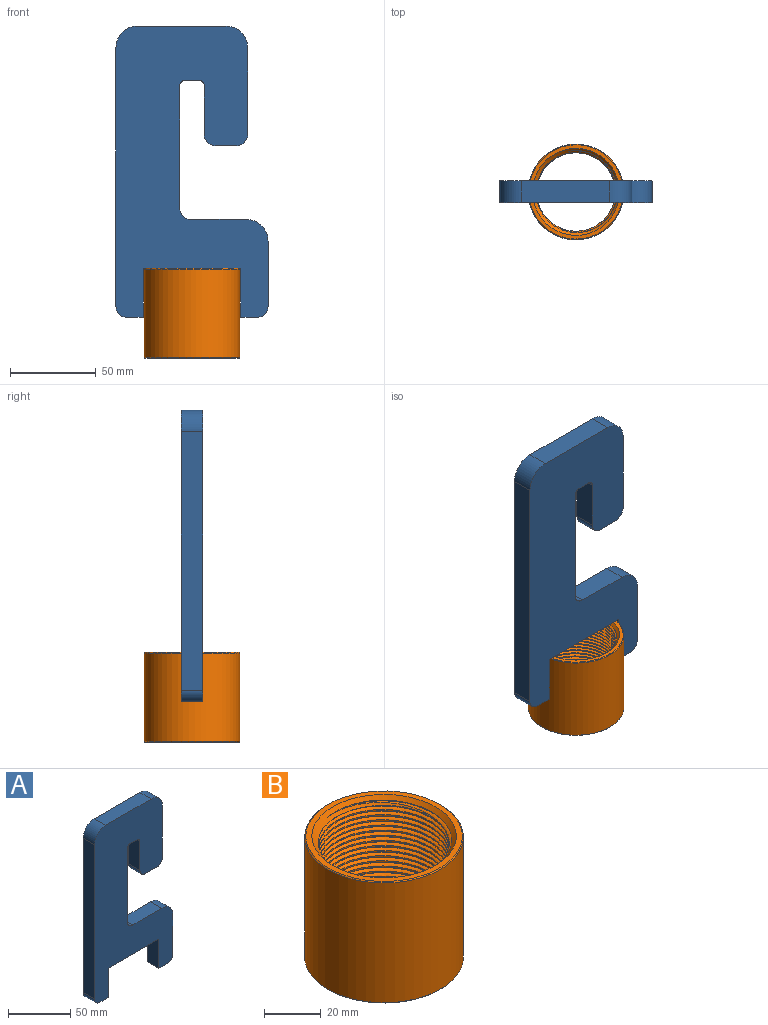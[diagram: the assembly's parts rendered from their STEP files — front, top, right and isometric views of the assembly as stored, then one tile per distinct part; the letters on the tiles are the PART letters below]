
ASSEMBLY  parts=2 mates=1
PART A: 26 faces, bbox 88.9x12.7x170.2 mm
  f0: plane 50.8x12.7mm, normal (1,0,0), area 645.2mm2, adj f1,f23,f24,f25
  f1: cylinder r=12.7mm len=12.7mm, axis (0,1,0), area 253.4mm2, adj f0,f2,f24,f25
  f2: plane 51.59x12.7mm, normal (0,0,1), area 655.2mm2, adj f1,f3,f24,f25
  f3: cylinder r=12.7mm len=12.7mm, axis (0,1,0), area 253.4mm2, adj f2,f4,f24,f25
  f4: plane 151.13x12.7mm, normal (-1,0,0), area 1919.4mm2, adj f3,f5,f24,f25
  f5: cylinder r=6.35mm len=12.7mm, axis (0,1,0), area 126.7mm2, adj f4,f6,f24,f25
  f6: plane 12.7x9.53mm, normal (0,0,-1), area 121mm2, adj f5,f7,f24,f25
  f7: plane 28.58x12.7mm, normal (1,0,0), area 362.9mm2, adj f6,f8,f24,f25
  f8: plane 57.15x12.7mm, normal (0,0,-1), area 725.8mm2, adj f7,f9,f24,f25
  f9: plane 28.58x12.7mm, normal (-1,0,0), area 362.9mm2, adj f8,f10,f24,f25
  f10: plane 12.7x9.53mm, normal (0,0,-1), area 121mm2, adj f9,f11,f24,f25
  f11: cylinder r=6.35mm len=12.7mm, axis (0,1,0), area 126.7mm2, adj f10,f12,f24,f25
  f12: plane 38.1x12.7mm, normal (1,0,0), area 483.9mm2, adj f11,f13,f24,f25
  f13: cylinder r=12.7mm len=12.7mm, axis (0,1,0), area 253.4mm2, adj f12,f14,f24,f25
  f14: plane 32.54x12.7mm, normal (0,0,1), area 413.3mm2, adj f13,f15,f24,f25
  f15: cylinder r=6.35mm len=12.7mm, axis (0,1,0), area 126.7mm2, adj f14,f16,f24,f25
  f16: plane 71.76x12.7mm, normal (1,0,0), area 911.3mm2, adj f15,f17,f24,f25
  f17: cylinder r=3.17mm len=12.7mm, axis (0,1,0), area 63.3mm2, adj f16,f18,f24,f25
  f18: plane 12.7x7.94mm, normal (0,0,-1), area 100.8mm2, adj f17,f19,f24,f25
  f19: cylinder r=3.17mm len=12.7mm, axis (0,1,0), area 63.3mm2, adj f18,f20,f24,f25
  f20: plane 28.58x12.7mm, normal (-1,0,0), area 362.9mm2, adj f19,f21,f24,f25
  f21: cylinder r=6.35mm len=12.7mm, axis (0,1,0), area 126.7mm2, adj f20,f22,f24,f25
  f22: plane 12.7x12.7mm, normal (0,0,-1), area 161.3mm2, adj f21,f23,f24,f25
  f23: cylinder r=6.35mm len=12.7mm, axis (0,1,0), area 126.7mm2, adj f0,f22,f24,f25
  f24: plane 170.18x88.9mm, normal (0,-1,0), area 9766.6mm2, adj f0,f1,f2,f3,f4,f5,f6,f7
  f25: plane 170.18x88.9mm, normal (0,1,0), area 9766.6mm2, adj f0,f1,f2,f3,f4,f5,f6,f7
PART B: 13 faces, bbox 55.9x55.9x52.4 mm
  f0: cone r=27.54mm half-angle=45deg, axis (0,0,-1), area 97.8mm2, adj f6,f12
  f1: cone r=27.94mm half-angle=45deg, axis (0,0,1), area 97.8mm2, adj f6,f11
  f2: cone r=25.4mm half-angle=40deg, axis (0,0,-1), area 453.9mm2, adj f3,f7,f8,f9,f10,f11
  f3: cone r=25.4mm half-angle=40deg, axis (0,0,-1), area 8.3mm2, adj f2,f7,f10
  f4: cone r=25.4mm half-angle=40deg, axis (0,0,1), area 461.5mm2, adj f5,f7,f8,f9,f10,f12
  f5: cone r=25.4mm half-angle=40deg, axis (0,0,1), area 1.2mm2, adj f4,f7,f9
  f6: cylinder r=27.94mm len=55.88mm, axis (0,0,-1), area 9055.2mm2, adj f0,f1
  f7: cylinder r=22.93mm len=46.5mm, axis (0,0,1), area 1675.1mm2, adj f2,f3,f4,f5,f9,f10
  f8: cylinder r=24.13mm len=49.35mm, axis (0,0,1), area 935.3mm2, adj f2,f4,f9,f10
  f9: bspline ~50.04x48.26mm, area 4430.1mm2, adj f2,f4,f5,f7,f8
  f10: bspline ~50.04x48.24mm, area 4429.6mm2, adj f2,f3,f4,f7,f8
  f11: plane 55.09x55.09mm, normal (0,0,-1), area 356.5mm2, adj f1,f2
  f12: plane 55.09x55.09mm, normal (0,0,1), area 356.5mm2, adj f0,f4
PLACE A t=(-127,6.35,44.35)mm
PLACE B at identity
MATE fastened A.f8 <-> B.f0  axis (0,0,-1) through (0,0,26.19)mm
